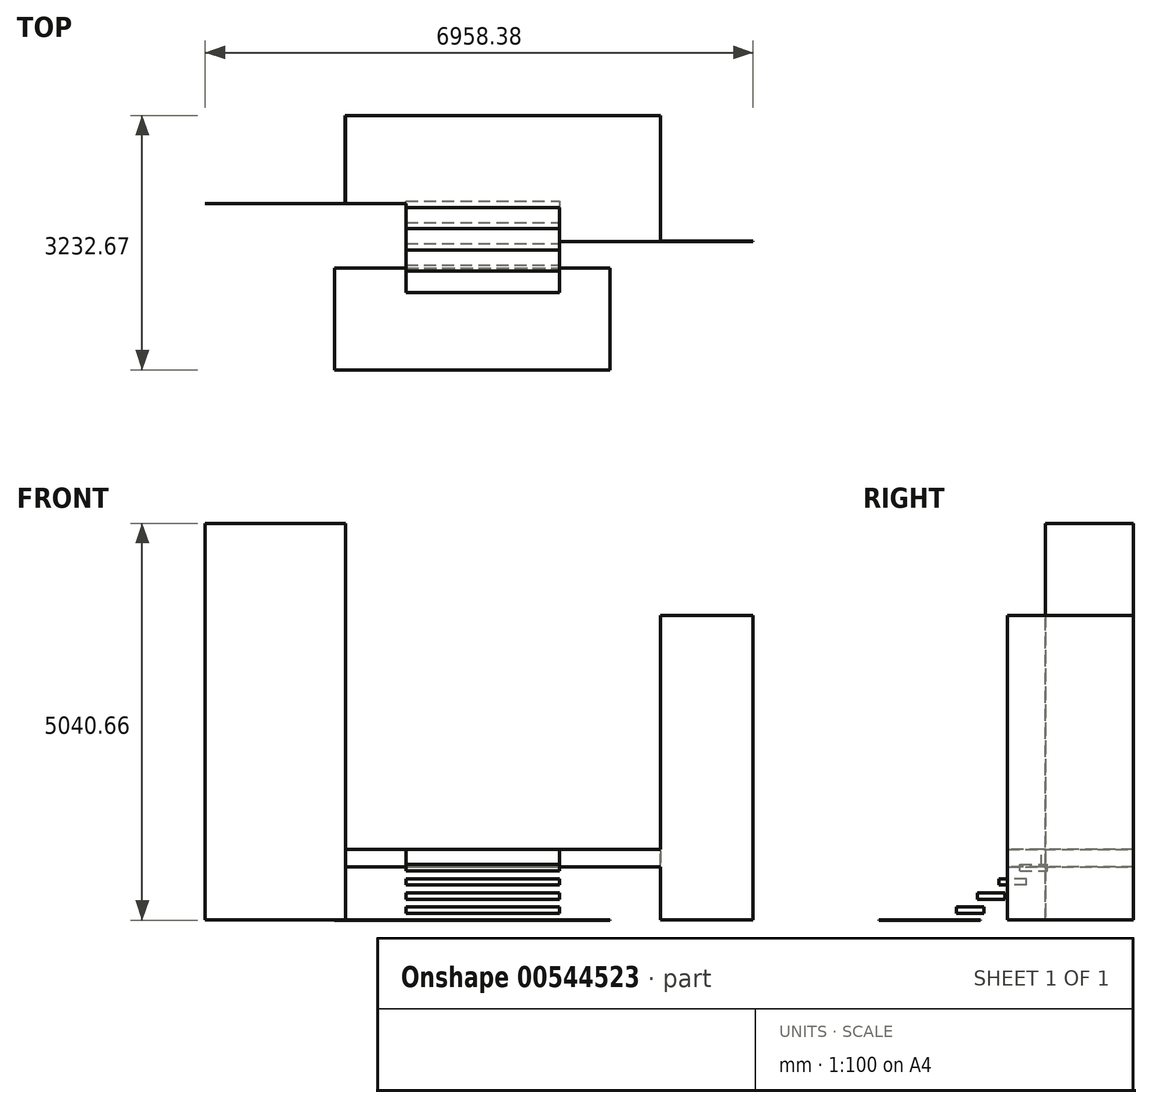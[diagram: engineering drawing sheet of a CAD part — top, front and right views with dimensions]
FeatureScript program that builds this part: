
annotation { "Feature Type Name" : "Feature", "Feature Type Description" : "" }
export const myFeature = defineFeature(function(context is Context, id is Id, definition is map)
    precondition{}
    {
        {
            var Q0;
            Q0=qCreatedBy(makeId("Top.planeOp"),FACE);
            var sketch = newSketch(context, id + "F0", { "sketchPlane" : qUnion([Q0])});
            skLineSegment(sketch, "E0", {"start": v(0, 0) * mm, "end": v(2000, 0) * mm});
            skLineSegment(sketch, "E1", {"start": v(0, 0) * mm, "end": v(-2000, 0) * mm});
            skLineSegment(sketch, "E2", {"start": v(-2000, 0) * mm, "end": v(-2000, -1120) * mm});
            skLineSegment(sketch, "E3", {"start": v(-2000, -1120) * mm, "end": v(-1230, -1120) * mm});
            skLineSegment(sketch, "E4", {"start": v(720, -1170) * mm, "end": v(720, -1600) * mm});
            skLineSegment(sketch, "E5", {"start": v(720, -1600) * mm, "end": v(2000, -1600) * mm});
            skLineSegment(sketch, "E6", {"start": v(2000, -1600) * mm, "end": v(2000, 0) * mm});
            skLineSegment(sketch, "E7", {"start": v(-1230, -1120) * mm, "end": v(-1230, -1170) * mm});
            skLineSegment(sketch, "E8", {"start": v(-1230, -1170) * mm, "end": v(720, -1170) * mm});
            skSolve(sketch);
        }
        {
            var Q0;
            Q0 = qSketchRegion(id + "F0", true);
            extrude(context, id + "F1", {"entities" : qUnion([Q0]), "oppositeDirection" : true, "depth" : (80 + 140) * mm, "offsetDistance" : 25 * mm});
        }
        {
            var Q0;
            Q0=makeQuery(id+"F1.opExtrude","CAP_FACE",FACE,{"disambiguationData":[OSD([sQuery(id+"F0.wireOp",EDGE,"E0"),sQuery(id+"F0.wireOp",EDGE,"E1"),sQuery(id+"F0.wireOp",EDGE,"E2"),sQuery(id+"F0.wireOp",EDGE,"E3"),sQuery(id+"F0.wireOp",EDGE,"E4"),sQuery(id+"F0.wireOp",EDGE,"E5"),sQuery(id+"F0.wireOp",EDGE,"E6"),sQuery(id+"F0.wireOp",EDGE,"E7"),sQuery(id+"F0.wireOp",EDGE,"E8")])],"isStart":true});
            cPlane(context, id + "F2", {"entities" : qUnion([Q0]), "cplaneType" : CPlaneType.OFFSET, "offset" : 190 * mm, "oppositeDirection" : true, "width" : 150 * mm, "height" : 150 * mm});
        }
        {
            var Q0;
            Q0=qCreatedBy(id+"F2.planeOp",FACE);
            cPlane(context, id + "F3", {"entities" : qUnion([Q0]), "cplaneType" : CPlaneType.OFFSET, "offset" : 180 * mm, "oppositeDirection" : true, "width" : 150 * mm, "height" : 150 * mm});
        }
        {
            var Q0;
            Q0=qCreatedBy(id+"F3.planeOp",FACE);
            cPlane(context, id + "F4", {"entities" : qUnion([Q0]), "cplaneType" : CPlaneType.OFFSET, "offset" : 180 * mm, "oppositeDirection" : true, "width" : 150 * mm, "height" : 150 * mm});
        }
        {
            var Q0;
            Q0=qCreatedBy(id+"F4.planeOp",FACE);
            cPlane(context, id + "F5", {"entities" : qUnion([Q0]), "cplaneType" : CPlaneType.OFFSET, "offset" : 180 * mm, "oppositeDirection" : true, "width" : 150 * mm, "height" : 150 * mm});
        }
        {
            var Q0;
            Q0=qCreatedBy(id+"F5.planeOp",FACE);
            cPlane(context, id + "F6", {"entities" : qUnion([Q0]), "cplaneType" : CPlaneType.OFFSET, "offset" : 165 * mm, "oppositeDirection" : true, "width" : 150 * mm, "height" : 150 * mm});
        }
        {
            var Q0;
            Q0=qCreatedBy(id+"F2.planeOp",FACE);
            var sketch = newSketch(context, id + "F7", { "sketchPlane" : qUnion([Q0])});
            skLineSegment(sketch, "E9", {"start": v(-1230, -1440) * mm, "end": v(-1230, -1090) * mm});
            skLineSegment(sketch, "E10", {"start": v(-1230, -1090) * mm, "end": v(720, -1090) * mm});
            skLineSegment(sketch, "E11", {"start": v(720, -1090) * mm, "end": v(720, -1440) * mm});
            skLineSegment(sketch, "E12", {"start": v(720, -1440) * mm, "end": v(-1230, -1440) * mm});
            skSolve(sketch);
        }
        {
            var Q0;
            Q0 = qSketchRegion(id + "F7", true);
            extrude(context, id + "F8", {"entities" : qUnion([Q0]), "oppositeDirection" : true, "depth" : 80 * mm, "offsetDistance" : 25 * mm});
        }
        {
            var Q0;
            Q0=qCreatedBy(id+"F3.planeOp",FACE);
            var sketch = newSketch(context, id + "F9", { "sketchPlane" : qUnion([Q0])});
            skLineSegment(sketch, "E13.bottom", {"start": v(-1230, -1360) * mm, "end": v(720, -1360) * mm});
            skLineSegment(sketch, "E13.top", {"start": v(-1230, -1710) * mm, "end": v(720, -1710) * mm});
            skLineSegment(sketch, "E13.left", {"start": v(-1230, -1360) * mm, "end": v(-1230, -1710) * mm});
            skLineSegment(sketch, "E13.right", {"start": v(720, -1360) * mm, "end": v(720, -1710) * mm});
            skSolve(sketch);
        }
        {
            var Q0;
            Q0 = qSketchRegion(id + "F9", true);
            extrude(context, id + "F10", {"entities" : qUnion([Q0]), "oppositeDirection" : true, "depth" : 80 * mm, "offsetDistance" : 25 * mm});
        }
        {
            var Q0;
            Q0=qCreatedBy(id+"F4.planeOp",FACE);
            var sketch = newSketch(context, id + "F11", { "sketchPlane" : qUnion([Q0])});
            skLineSegment(sketch, "E14.bottom", {"start": v(-1230, -1630) * mm, "end": v(720, -1630) * mm});
            skLineSegment(sketch, "E14.top", {"start": v(-1230, -1980) * mm, "end": v(720, -1980) * mm});
            skLineSegment(sketch, "E14.left", {"start": v(-1230, -1630) * mm, "end": v(-1230, -1980) * mm});
            skLineSegment(sketch, "E14.right", {"start": v(720, -1630) * mm, "end": v(720, -1980) * mm});
            skSolve(sketch);
        }
        {
            var Q0;
            Q0 = qSketchRegion(id + "F11", true);
            extrude(context, id + "F12", {"entities" : qUnion([Q0]), "oppositeDirection" : true, "depth" : 80 * mm, "offsetDistance" : 25 * mm});
        }
        {
            var Q0;
            Q0=qCreatedBy(id+"F5.planeOp",FACE);
            var sketch = newSketch(context, id + "F13", { "sketchPlane" : qUnion([Q0])});
            skLineSegment(sketch, "E15.bottom", {"start": v(-1230, -1900) * mm, "end": v(720, -1900) * mm});
            skLineSegment(sketch, "E15.top", {"start": v(-1230, -2250) * mm, "end": v(720, -2250) * mm});
            skLineSegment(sketch, "E15.left", {"start": v(-1230, -1900) * mm, "end": v(-1230, -2250) * mm});
            skLineSegment(sketch, "E15.right", {"start": v(720, -1900) * mm, "end": v(720, -2250) * mm});
            skSolve(sketch);
        }
        {
            var Q0;
            Q0 = qSketchRegion(id + "F13", true);
            extrude(context, id + "F14", {"entities" : qUnion([Q0]), "oppositeDirection" : true, "depth" : 80 * mm, "offsetDistance" : 25 * mm});
        }
        {
            var Q0;
            Q0=qCreatedBy(id+"F6.planeOp",FACE);
            var sketch = newSketch(context, id + "F15", { "sketchPlane" : qUnion([Q0])});
            skLineSegment(sketch, "E16.bottom", {"start": v(-2139.48, -1941.5) * mm, "end": v(1358.5, -1941.5) * mm});
            skLineSegment(sketch, "E16.top", {"start": v(-2139.48, -3232.67) * mm, "end": v(1358.5, -3232.67) * mm});
            skLineSegment(sketch, "E16.left", {"start": v(-2139.48, -1941.5) * mm, "end": v(-2139.48, -3232.67) * mm});
            skLineSegment(sketch, "E16.right", {"start": v(1358.5, -1941.5) * mm, "end": v(1358.5, -3232.67) * mm});
            skSolve(sketch);
        }
        {
            var Q0;
            Q0 = qSketchRegion(id + "F15", true);
            extrude(context, id + "F16", {"entities" : qUnion([Q0]), "oppositeDirection" : true, "depth" : 1 * mm, "offsetDistance" : 25 * mm});
        }
        {
            var Q0;
            Q0=makeQuery(id+"F1.opExtrude","SWEPT_FACE",FACE,{"disambiguationData":[OSD([sQuery(id+"F0.wireOp",EDGE,"E2")])]});
            var sketch = newSketch(context, id + "F17", { "sketchPlane" : qUnion([Q0])});
            skLineSegment(sketch, "E17", {"start": v(1120, -895) * mm, "end": v(1120, 4144.66) * mm});
            skLineSegment(sketch, "E18", {"start": v(1120, 4144.66) * mm, "end": v(0, 4144.66) * mm});
            skLineSegment(sketch, "E19", {"start": v(0, 4144.66) * mm, "end": v(0, -895) * mm});
            skLineSegment(sketch, "E20", {"start": v(0, -895) * mm, "end": v(1120, -895) * mm});
            skSolve(sketch);
        }
        {
            var Q0;
            Q0 = qSketchRegion(id + "F17", true);
            extrude(context, id + "F18", {"entities" : qUnion([Q0]), "operationType" : NewBodyOperationType.ADD, "depth" : 1 * mm, "offsetDistance" : 25 * mm});
        }
        {
            var Q0;
            Q0=makeQuery(id+"F18.boolean.opBoolean","MERGE",FACE,{"derivedFrom":[makeQuery(id+"F1.opExtrude","SWEPT_FACE",FACE,{"disambiguationData":[OSD([sQuery(id+"F0.wireOp",EDGE,"E3")])]}),makeQuery(id+"F18.opExtrude","SWEPT_FACE",FACE,{"disambiguationData":[OSD([sQuery(id+"F17.wireOp",EDGE,"E17")])]})]});
            var sketch = newSketch(context, id + "F19", { "sketchPlane" : qUnion([Q0])});
            skLineSegment(sketch, "E21.bottom", {"start": v(-2000, 4144.66) * mm, "end": v(-3780.5, 4144.66) * mm});
            skLineSegment(sketch, "E21.top", {"start": v(-2000, -895) * mm, "end": v(-3780.5, -895) * mm});
            skLineSegment(sketch, "E21.left", {"start": v(-2000, 4144.66) * mm, "end": v(-2000, -895) * mm});
            skLineSegment(sketch, "E21.right", {"start": v(-3780.5, 4144.66) * mm, "end": v(-3780.5, -895) * mm});
            skSolve(sketch);
        }
        {
            var Q0;
            Q0 = qSketchRegion(id + "F19", true);
            extrude(context, id + "F20", {"entities" : qUnion([Q0]), "operationType" : NewBodyOperationType.ADD, "depth" : 1 * mm, "offsetDistance" : 25 * mm});
        }
        {
            var Q0;
            Q0=makeQuery(id+"F1.opExtrude","SWEPT_FACE",FACE,{"disambiguationData":[OSD([sQuery(id+"F0.wireOp",EDGE,"E6")])]});
            var sketch = newSketch(context, id + "F21", { "sketchPlane" : qUnion([Q0])});
            skLineSegment(sketch, "E22", {"start": v(-1600, 2973.23) * mm, "end": v(-1600, -895) * mm});
            skLineSegment(sketch, "E23", {"start": v(-1600, -895) * mm, "end": v(0, -895) * mm});
            skLineSegment(sketch, "E24", {"start": v(0, -895) * mm, "end": v(0, 2973.23) * mm});
            skLineSegment(sketch, "E25", {"start": v(0, 2973.23) * mm, "end": v(-1600, 2973.23) * mm});
            skSolve(sketch);
        }
        {
            var Q0;
            Q0 = qSketchRegion(id + "F21", true);
            extrude(context, id + "F22", {"entities" : qUnion([Q0]), "operationType" : NewBodyOperationType.ADD, "depth" : 1 * mm, "offsetDistance" : 25 * mm});
        }
        {
            var Q0;
            Q0=makeQuery(id+"F22.boolean.opBoolean","MERGE",FACE,{"derivedFrom":[makeQuery(id+"F1.opExtrude","SWEPT_FACE",FACE,{"disambiguationData":[OSD([sQuery(id+"F0.wireOp",EDGE,"E5")])]}),makeQuery(id+"F22.opExtrude","SWEPT_FACE",FACE,{"disambiguationData":[OSD([sQuery(id+"F21.wireOp",EDGE,"E22")])]})]});
            var sketch = newSketch(context, id + "F23", { "sketchPlane" : qUnion([Q0])});
            skLineSegment(sketch, "E26.bottom", {"start": v(2000, 2973.23) * mm, "end": v(3176.88, 2973.54) * mm});
            skLineSegment(sketch, "E26.top", {"start": v(2001, -895) * mm, "end": v(3177.88, -894.7) * mm});
            skLineSegment(sketch, "E26.left", {"start": v(2000, 2973.23) * mm, "end": v(2001, -895) * mm});
            skLineSegment(sketch, "E26.right", {"start": v(3176.88, 2973.54) * mm, "end": v(3177.88, -894.7) * mm});
            skSolve(sketch);
        }
        {
            var Q0;
            Q0 = qSketchRegion(id + "F23", true);
            extrude(context, id + "F24", {"entities" : qUnion([Q0]), "operationType" : NewBodyOperationType.ADD, "oppositeDirection" : true, "depth" : 1 * mm, "offsetDistance" : 25 * mm});
        }
    });
